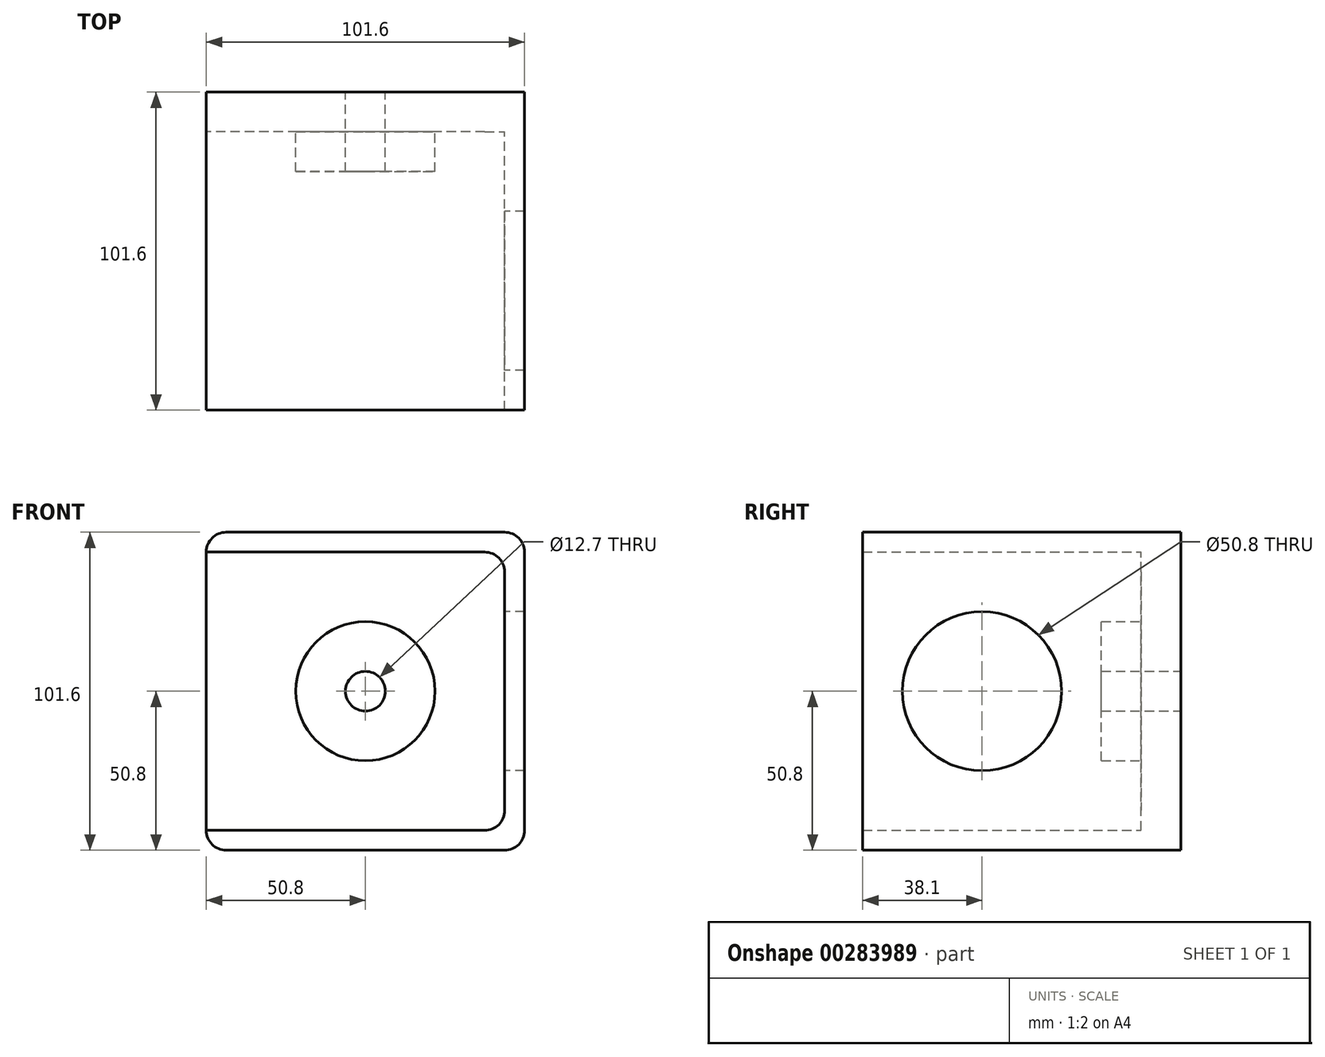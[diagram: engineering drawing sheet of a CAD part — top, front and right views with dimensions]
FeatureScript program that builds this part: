
annotation { "Feature Type Name" : "Feature", "Feature Type Description" : "" }
export const myFeature = defineFeature(function(context is Context, id is Id, definition is map)
    precondition{}
    {
        {
            var Q0;
            Q0=qCreatedBy(makeId("Front.planeOp"),FACE);
            var sketch = newSketch(context, id + "F0", { "sketchPlane" : qUnion([Q0])});
            skLineSegment(sketch, "E0.bottom", {"start": v(44.45, -50.8) * mm, "end": v(-44.45, -50.8) * mm});
            skLineSegment(sketch, "E0.top", {"start": v(44.45, 50.8) * mm, "end": v(-44.45, 50.8) * mm});
            skLineSegment(sketch, "E0.left", {"start": v(50.8, -44.45) * mm, "end": v(50.8, 44.45) * mm});
            skLineSegment(sketch, "E0.right", {"start": v(-50.8, -44.45) * mm, "end": v(-50.8, 44.45) * mm});
            skPoint(sketch, "E0.middle", {"position": v(0, 0) * mm});
            skLineSegment(sketch, "E1", {"start": v(-50.8, 44.45) * mm, "end": v(38.1, 44.45) * mm});
            skLineSegment(sketch, "E2", {"start": v(44.45, 38.1) * mm, "end": v(44.45, -38.1) * mm});
            skLineSegment(sketch, "E3", {"start": v(38.1, -44.45) * mm, "end": v(-50.8, -44.45) * mm});
            skPoint(sketch, "E4.visualSharp", {"position": v(-50.8, -50.8) * mm});
            skArc(sketch, "E4.filletArc", {"start": v(-50.8, -44.45) * mm, "mid": v(-48.94, -48.94) * mm, "end": v(-44.45, -50.8) * mm});
            skPoint(sketch, "E5.visualSharp", {"position": v(-50.8, 50.8) * mm});
            skArc(sketch, "E5.filletArc", {"start": v(-44.45, 50.8) * mm, "mid": v(-48.94, 48.94) * mm, "end": v(-50.8, 44.45) * mm});
            skPoint(sketch, "E6.visualSharp", {"position": v(50.8, 50.8) * mm});
            skArc(sketch, "E6.filletArc", {"start": v(50.8, 44.45) * mm, "mid": v(48.94, 48.94) * mm, "end": v(44.45, 50.8) * mm});
            skArc(sketch, "E7.filletArc", {"start": v(44.45, 38.1) * mm, "mid": v(42.6, 42.6) * mm, "end": v(38.1, 44.45) * mm});
            skPoint(sketch, "E8.visualSharp", {"position": v(44.45, -44.45) * mm});
            skArc(sketch, "E8.filletArc", {"start": v(38.1, -44.45) * mm, "mid": v(42.6, -42.6) * mm, "end": v(44.45, -38.1) * mm});
            skPoint(sketch, "E9.visualSharp", {"position": v(50.8, -50.8) * mm});
            skArc(sketch, "E9.filletArc", {"start": v(44.45, -50.8) * mm, "mid": v(48.94, -48.94) * mm, "end": v(50.8, -44.45) * mm});
            skCircle(sketch, "E10", {"center": v(0, 0) * mm, "radius": 22.23 * mm});
            skCircle(sketch, "E11", {"center": v(0, 0) * mm, "radius": 6.35 * mm});
            skSolve(sketch);
        }
        {
            var Q0;
            {var subQ0=sQuery(id+"F0.wireOp",EDGE,"E1");Q0=makeQuery(id+"F0.imprint","IMPRINT",FACE,{"disambiguationData":[TD([[makeQuery(id+"F0.imprint","IMPRINT",EDGE,{"derivedFrom":subQ0}),-1.0]])]});}
            extrude(context, id + "F1", {"entities" : qUnion([Q0]), "depth" : 12.7 * mm});
        }
        {
            var Q0;
            {var subQ1=sQuery(id+"F0.wireOp",EDGE,"E0.bottom");Q0=makeQuery(id+"F0.imprint","IMPRINT",FACE,{"disambiguationData":[TD([[makeQuery(id+"F0.imprint","IMPRINT",EDGE,{"derivedFrom":subQ1}),-1.0]])]});}
            extrude(context, id + "F2", {"entities" : qUnion([Q0]), "operationType" : NewBodyOperationType.ADD, "depth" : 101.6 * mm});
        }
        {
            var Q0;
            Q0=makeQuery(id+"F0.imprint","IMPRINT",FACE,{"disambiguationData":[TD([[makeQuery(id+"F0.imprint","IMPRINT",EDGE,{"derivedFrom":sQuery(id+"F0.wireOp",EDGE,"E10")}),1.0]])]});
            extrude(context, id + "F3", {"entities" : qUnion([Q0]), "operationType" : NewBodyOperationType.ADD, "depth" : 25.4 * mm});
        }
        {
            var Q0;
            Q0=makeQuery(id+"F2.opExtrude","SWEPT_FACE",FACE,{"disambiguationData":[OSD([sQuery(id+"F0.wireOp",EDGE,"E2")])]});
            var sketch = newSketch(context, id + "F4", { "sketchPlane" : qUnion([Q0])});
            skCircle(sketch, "E12", {"center": v(63.5, 0) * mm, "radius": 25.4 * mm});
            skSolve(sketch);
        }
        {
            var Q0;
            Q0=makeQuery(id+"F4.imprint","IMPRINT",FACE,{"disambiguationData":[TD([[makeQuery(id+"F4.imprint","IMPRINT",EDGE,{"derivedFrom":sQuery(id+"F4.wireOp",EDGE,"E12")}),1.0]])]});
            extrude(context, id + "F5", {"entities" : qUnion([Q0]), "operationType" : NewBodyOperationType.REMOVE, "endBound" : BoundingType.THROUGH_ALL, "oppositeDirection" : true, "depth" : 25.4 * mm});
        }
    });
